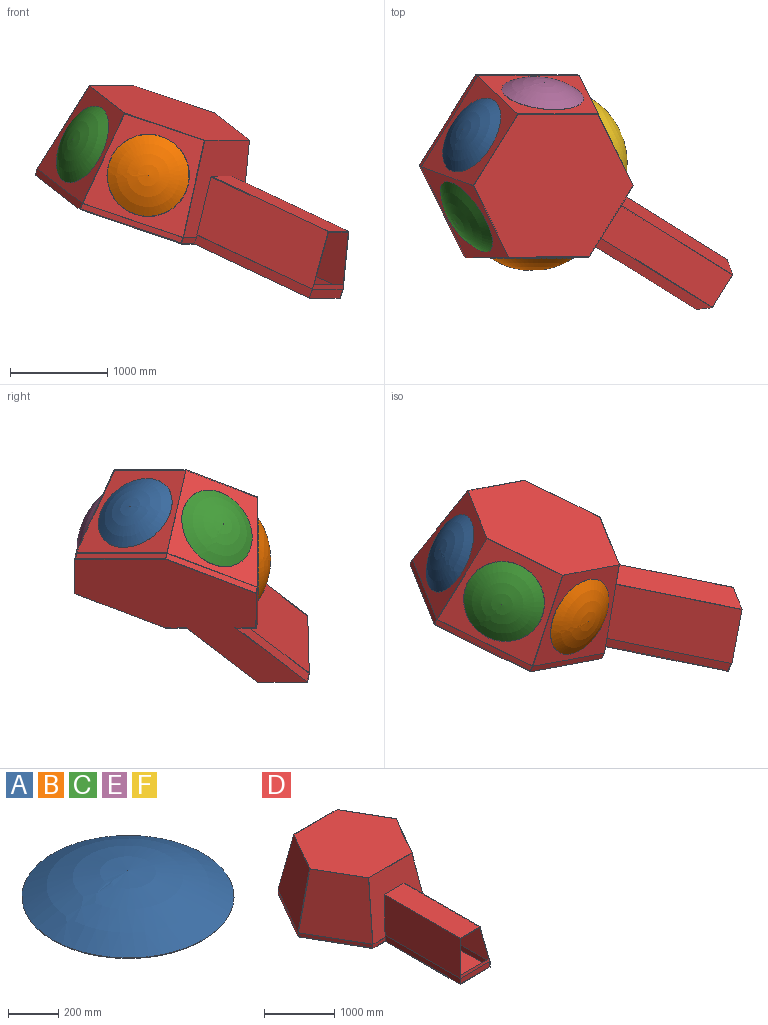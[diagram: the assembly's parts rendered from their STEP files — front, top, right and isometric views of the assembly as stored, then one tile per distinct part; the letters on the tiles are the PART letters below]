
ASSEMBLY  parts=6 mates=5
PART A: 3 faces, bbox 846.6x846.6x132 mm
  f0: cone r=420mm half-angle=33.4deg, axis (0,0,1), area 15895.9mm2, adj f1,f2
  f1: sphere r=763mm, area 604052.9mm2, adj f0
  f2: sphere r=769mm, area 613590.4mm2, adj f0
PART B: same geometry as A
PART C: same geometry as A
PART D: 43 faces, bbox 2200x3405.3x1070 mm
  f0: plane 250x70mm, normal (0,-1,0), area 17500mm2, adj f3,f7,f10,f14
  f1: plane 250x70mm, normal (0,-1,0), area 17500mm2, adj f2,f7,f9,f14
  f2: plane 952.63x550mm, normal (-0.87,-0.5,0), area 77000mm2, adj f1,f6,f7,f13
  f3: plane 952.63x550mm, normal (0.87,-0.5,0), area 77000mm2, adj f0,f4,f7,f16
  f4: plane 952.63x550mm, normal (0.87,0.5,0), area 77000mm2, adj f3,f5,f7,f18
  f5: plane 1100x70mm, normal (0,1,0), area 77000mm2, adj f4,f6,f7,f17
  f6: plane 952.63x550mm, normal (-0.87,0.5,0), area 77000mm2, adj f2,f5,f7,f15
  f7: plane 3405.26x2200mm, normal (0,0,-1), area 4043672.2mm2, adj f0,f1,f2,f3,f4,f5,f6,f9
  f8: plane 1738.12x1505.26mm, normal (0,0,1), area 1962236.3mm2, adj f13,f14,f15,f16,f17,f18
  f9: plane 1506x100mm, normal (-1,0,0), area 150090mm2, adj f1,f7,f11,f14,f19
  f10: plane 1506x100mm, normal (1,0,0), area 150090mm2, adj f0,f7,f11,f14,f20
  f11: plane 600x100mm, normal (0,-1,0), area 60000mm2, adj f7,f9,f10,f21
  f12: plane 1526x400mm, normal (0,0,1), area 610400mm2, adj f14,f19,f20,f21
  f13: plane 1000x952.63mm, normal (-0.85,-0.49,0.2), area 1004027.5mm2, adj f2,f8,f14,f15
  f14: plane 1100x1000mm, normal (0,-0.98,0.2), area 679729.8mm2, adj f0,f1,f8,f9,f10,f12,f13,f16
  f15: plane 1000x952.63mm, normal (-0.85,0.49,0.2), area 1004027.5mm2, adj f6,f8,f13,f17
  f16: plane 1000x952.63mm, normal (0.85,-0.49,0.2), area 1004027.5mm2, adj f3,f8,f14,f18
  f17: plane 1100x1000mm, normal (0,0.98,0.2), area 1004027.5mm2, adj f5,f8,f15,f18
  f18: plane 1000x952.63mm, normal (0.85,0.49,0.2), area 1004027.5mm2, adj f4,f8,f16,f17
  f19: plane 1626x600mm, normal (-0.99,0,0.16), area 922146.8mm2, adj f9,f12,f14,f21
  f20: plane 1626x600mm, normal (0.99,0,0.16), area 922146.8mm2, adj f10,f12,f14,f21
  f21: plane 600x600mm, normal (0,-0.99,0.16), area 41008.7mm2, adj f11,f12,f19,f20,f33,f34,f41,f42
  f22: plane 253.38x61.21mm, normal (0,1,0), area 15508.9mm2, adj f25,f29,f32,f36
  f23: plane 253.38x61.21mm, normal (0,1,0), area 15508.9mm2, adj f24,f29,f31,f36
  f24: plane 944.63x545.38mm, normal (0.87,0.5,0), area 66763.2mm2, adj f23,f28,f29,f35
  f25: plane 944.63x545.38mm, normal (-0.87,0.5,0), area 66763.2mm2, adj f22,f26,f29,f38
  f26: plane 944.63x545.38mm, normal (-0.87,-0.5,0), area 66763.2mm2, adj f25,f27,f29,f40
  f27: plane 1090.76x61.21mm, normal (0,-1,0), area 66763.2mm2, adj f26,f28,f29,f39
  f28: plane 944.63x545.38mm, normal (0.87,-0.5,0), area 66763.2mm2, adj f24,f27,f29,f37
  f29: plane 3389.26x2181.52mm, normal (0,0,1), area 3967093.9mm2, adj f22,f23,f24,f25,f26,f27,f28,f31
  f30: plane 1722.97x1492.14mm, normal (0,0,-1), area 1928187.3mm2, adj f35,f36,f37,f38,f39,f40
  f31: plane 1506.03x91.34mm, normal (1,0,0), area 137097.6mm2, adj f23,f29,f33,f36,f41
  f32: plane 1506.03x91.34mm, normal (-1,0,0), area 137097.6mm2, adj f22,f29,f33,f36,f42
  f33: plane 584x140mm, normal (0,1,0), area 81365.3mm2, adj f21,f29,f31,f32,f41,f42
  f34: plane 1533.89x386.45mm, normal (0,0,-1), area 592766.3mm2, adj f21,f36,f41,f42
  f35: plane 992.79x944.63mm, normal (0.85,0.49,-0.2), area 988280.6mm2, adj f24,f30,f36,f37
  f36: plane 1090.76x992.79mm, normal (0,0.98,-0.2), area 677067.9mm2, adj f22,f23,f30,f31,f32,f34,f35,f38
  f37: plane 992.79x944.63mm, normal (0.85,-0.49,-0.2), area 988280.6mm2, adj f28,f30,f35,f39
  f38: plane 992.79x944.63mm, normal (-0.85,0.49,-0.2), area 988280.6mm2, adj f25,f30,f36,f40
  f39: plane 1090.76x992.79mm, normal (0,-0.98,-0.2), area 988280.6mm2, adj f27,f30,f37,f40
  f40: plane 992.79x944.63mm, normal (-0.85,-0.49,-0.2), area 988280.6mm2, adj f26,f30,f38,f39
  f41: plane 1624.56x592.66mm, normal (0.99,0,-0.16), area 915484.2mm2, adj f21,f31,f33,f34,f36
  f42: plane 1624.56x592.66mm, normal (-0.99,0,-0.16), area 915484.2mm2, adj f21,f32,f33,f34,f36
PART E: same geometry as A
PART F: same geometry as A
PLACE A rot(axis=(-0.65,-0.36,0.67),79.5deg) t=(-622.5,1172.72,460.48)mm
PLACE B rot(axis=(1,0,0),90deg) t=(-4.74,-84.92,-13.95)mm
PLACE C rot(axis=(0.59,-0.8,-0.06),68.8deg) t=(-676.22,337.63,302.34)mm
PLACE D rot(axis=(0.32,0.18,0.93),61.7deg) t=(-124.32,862.94,-365.98)mm fixed
PLACE E rot(axis=(-0.85,0.37,0.37),74.7deg) t=(103.32,1594.89,304.16)mm
PLACE F rot(axis=(-0.75,0.47,-0.47),106.2deg) t=(774.18,1172.72,-13.95)mm
MATE fastened E.f0 <-> D.f18  axis (-0.12,-0.92,-0.36) through (103.32,1594.89,304.16)mm
MATE fastened D.f16 <-> F.f0  axis (0.9,0.44,0) through (778.67,1174.94,-13.95)mm
MATE fastened C.f0 <-> D.f15  axis (-0.77,-0.52,0.36) through (-680.09,335.03,304.16)mm
MATE fastened D.f17 <-> A.f0  axis (-0.71,0.44,0.55) through (-626.06,1174.94,463.22)mm
MATE fastened D.f13 <-> B.f0  axis (0,-1,0) through (-4.74,-84.92,-13.95)mm
